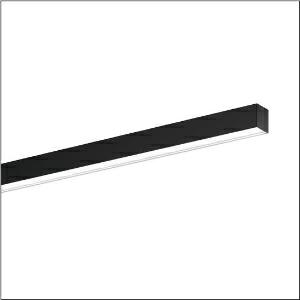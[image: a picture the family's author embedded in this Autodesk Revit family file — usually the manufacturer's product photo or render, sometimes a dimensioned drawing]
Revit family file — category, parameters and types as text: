
# Revit family: silica_r__21_51mx20da32bb_5abe
name_source: partatom
category: Lighting Fixtures
units: mm (PartAtom-declared; Revit-internal decimal feet)

## family parameters
Cut with Voids When Loaded = No
Host = Face
Light Source = No
Part Type = Normal
Room Calculation Point = No
Round Connector Dimension = Use Diameter
Shared = No

## types (1)
- --- (1 x LED, 2400 lm, 16.1 W, 3000K)
    Apparent Load = 16 VA
    CIE Flux Codes = 48 79 96 100 100
    Color Rendering = 80
    Color Temperature = 3000K
    Default Elevation = 1800 mm
    Description = Silica® 21, office luminaire, primary optical cover: cover, of PMMA, opal, light emission: direct distribution, primary light characteristic: symmetric, installation type: surface-mounted, LED, rated luminous flux: 2.400lm, luminous efficacy: 149lm/W, light colour: 830, colour temperature: 3000K, with terminal, 3+2-pole, max. 2.5mm², mains connection: 220..240V, AC, 50/60Hz, rated input power: 16.1W, luminaire housing, of aluminium, jet black (RAL 9005), length: 1.204mm, width: 53mm, height: 53mm, protection rating (complete): IP20, insulation class (complete): insulation class I (protective earthing), certification: CE, permissible operating ambient temperature: 0..+35°C, standard: EN 50419, packaging unit: 1 piece
    Height = 0 mm  [stored 0 ft]
    Lamp = 1 x LED
    Lamp Light Flux = 2400 lm
    Lamp Power = 16.1 W
    Lamp count = 1
    Length = 1204 mm
    Luminous efficacy = 149 lm/W
    Manufacturer = Siteco
    ModVariant = No
    Model = 51MX20DA32BB
    Mounting Place = Ceiling
    Mounting Type = Recessed
    Number of Poles = 1
    OnlyDefault = Yes
    Power Factor = 1
    Product Name = Silica® 21
    Product group = office luminaire | ceiling recessed
    ProductGroupID = 400
    Protection Class = Protection class I
    Protection Degree = IP 20
    RLX_Detail_Level = 1
    RLX_Emergency_Light_Flux = 0 lm
    RLX_Emergency_Type = 0
    RLX_Emergency_Type_DB = No
    RlxData = <blob elided: 28725 chars, md5=619c527e>
    Socket = socket
    Standby Power = 0 W
    System Light Flux = 2400 lm
    System Power = 16 W
    Type Comments = factory setting: luminous flux: 100 % | dim-lin: 254 | 233 mA
    Type Image = l_1335925.jpg
    URL = http://relux.com
    VarID = @adj_087137
    Voltage = 0 V
    Weight = 0.00 kg
    Width = 53 mm

note: [stored X ft] marks values corroborated as IEEE doubles in the binary element streams (Revit-internal decimal feet)

## geometry (parser evidence)
native form markers: Blend x4, Sweep x9
no freeform markers — native parametric forms only
